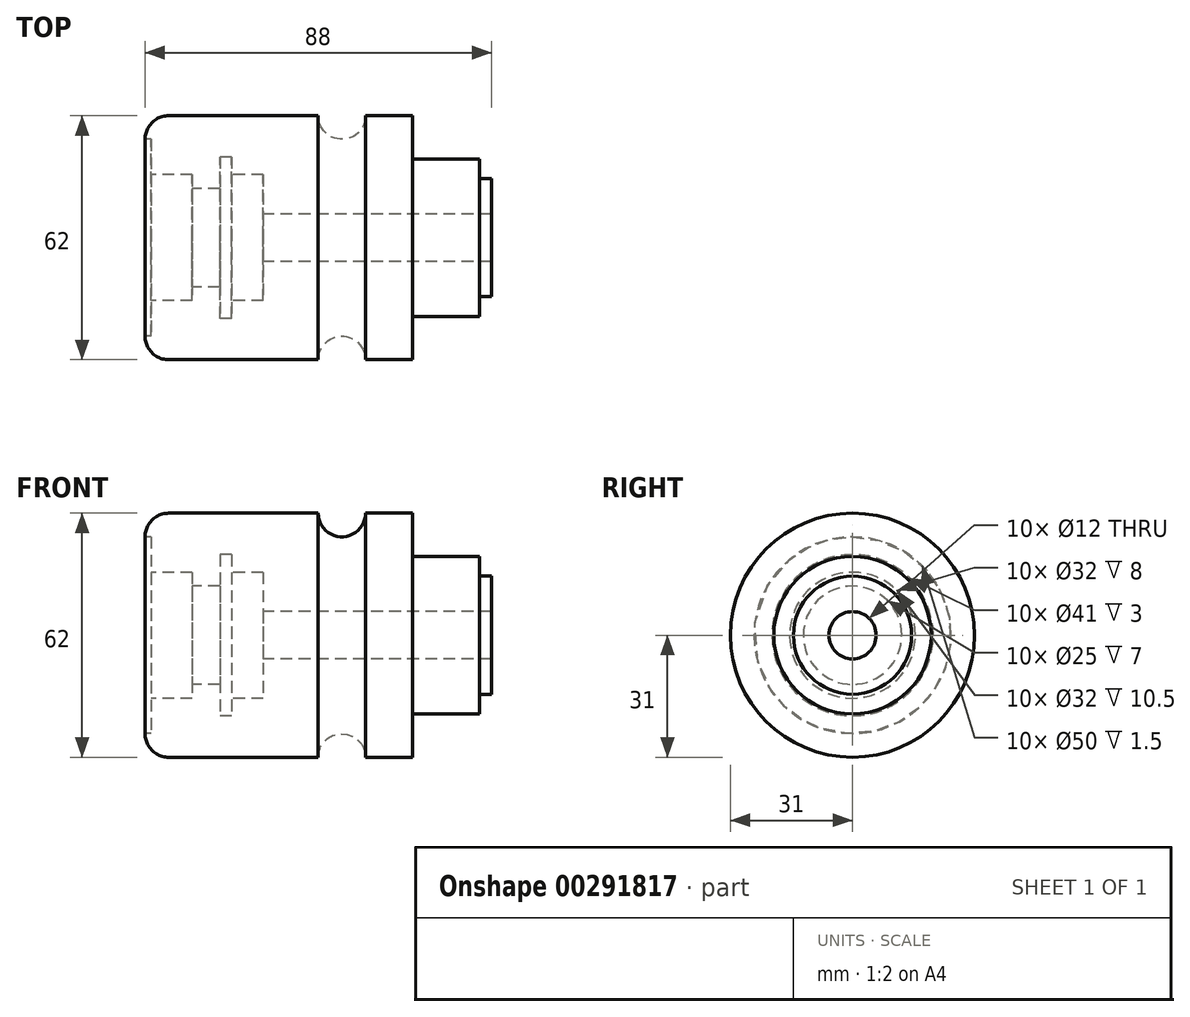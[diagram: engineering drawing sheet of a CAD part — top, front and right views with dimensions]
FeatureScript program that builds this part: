
annotation { "Feature Type Name" : "Feature", "Feature Type Description" : "" }
export const myFeature = defineFeature(function(context is Context, id is Id, definition is map)
    precondition{}
    {
        {
            var Q0;
            Q0=qCreatedBy(makeId("Front.planeOp"),FACE);
            var sketch = newSketch(context, id + "F0", { "sketchPlane" : qUnion([Q0])});
            skLineSegment(sketch, "E0", {"start": v(0, 0) * mm, "end": v(90.92, 0) * mm, "construction": true});
            skLineSegment(sketch, "E1", {"start": v(0, 0) * mm, "end": v(0, 31) * mm});
            skLineSegment(sketch, "E2", {"start": v(0, 31) * mm, "end": v(44, 31) * mm});
            skLineSegment(sketch, "E3", {"start": v(68, 31) * mm, "end": v(68, 20) * mm});
            skLineSegment(sketch, "E4", {"start": v(68, 20) * mm, "end": v(85, 20) * mm});
            skLineSegment(sketch, "E5", {"start": v(85, 20) * mm, "end": v(85, 15) * mm});
            skLineSegment(sketch, "E6", {"start": v(85, 15) * mm, "end": v(88, 15) * mm});
            skLineSegment(sketch, "E7", {"start": v(88, 15) * mm, "end": v(88, 0) * mm});
            skArc(sketch, "E8", {"start": v(44, 31) * mm, "mid": v(50, 25) * mm, "end": v(56, 31) * mm});
            skLineSegment(sketch, "E9.trimOffspring", {"start": v(56, 31) * mm, "end": v(68, 31) * mm});
            skLineSegment(sketch, "E10", {"start": v(88, 0) * mm, "end": v(0, 0) * mm});
            skSolve(sketch);
        }
        {
            var Q0;
            Q0 = qSketchRegion(id + "F0", true);
            var Q1;
            Q1=sQuery(id+"F0.wireOp",EDGE,"E0");
            revolve(context, id + "F1", {"entities" : qUnion([Q0]), "axis" : qUnion([Q1]), "revolveType" : RevolveType.FULL});
        }
        {
            var Q0;
            Q0=qCreatedBy(makeId("Front.planeOp"),FACE);
            var sketch = newSketch(context, id + "F2", { "sketchPlane" : qUnion([Q0])});
            skLineSegment(sketch, "E11", {"start": v(0, 0) * mm, "end": v(0, 25) * mm});
            skLineSegment(sketch, "E12", {"start": v(0, 25) * mm, "end": v(1.5, 25) * mm});
            skLineSegment(sketch, "E13", {"start": v(1.5, 25) * mm, "end": v(1.5, 16) * mm});
            skLineSegment(sketch, "E14", {"start": v(1.5, 16) * mm, "end": v(12, 16) * mm});
            skLineSegment(sketch, "E15", {"start": v(12, 16) * mm, "end": v(12, 12.5) * mm});
            skLineSegment(sketch, "E16", {"start": v(12, 12.5) * mm, "end": v(19, 12.5) * mm});
            skLineSegment(sketch, "E17", {"start": v(19, 12.5) * mm, "end": v(19, 20.5) * mm});
            skLineSegment(sketch, "E18", {"start": v(19, 20.5) * mm, "end": v(22, 20.5) * mm});
            skLineSegment(sketch, "E19", {"start": v(22, 20.5) * mm, "end": v(22, 16) * mm});
            skLineSegment(sketch, "E20", {"start": v(22, 16) * mm, "end": v(30, 16) * mm});
            skLineSegment(sketch, "E21", {"start": v(30, 16) * mm, "end": v(30, 6) * mm});
            skLineSegment(sketch, "E22", {"start": v(30, 6) * mm, "end": v(88, 6) * mm});
            skLineSegment(sketch, "E23", {"start": v(88, 6) * mm, "end": v(88, 0) * mm});
            skLineSegment(sketch, "E24", {"start": v(88, 0) * mm, "end": v(0, 0) * mm});
            skLineSegment(sketch, "E25", {"start": v(0, 0) * mm, "end": v(-15.84, 0) * mm, "construction": true});
            skSolve(sketch);
        }
        {
            var Q0;
            Q0 = qSketchRegion(id + "F2", true);
            var Q1;
            Q1=sQuery(id+"F2.wireOp",EDGE,"E25");
            revolve(context, id + "F3", {"operationType" : NewBodyOperationType.REMOVE, "entities" : qUnion([Q0]), "axis" : qUnion([Q1]), "revolveType" : RevolveType.FULL, "oppositeDirection" : true});
        }
        {
            var Q0;
            Q0=makeQuery(id+"F1.opRevolve","SWEPT_EDGE",EDGE,{"disambiguationData":[OSD([sQuery(id+"F0.wireOp",EDGE,"E1"),sQuery(id+"F0.wireOp",EDGE,"E2")])]});
            fillet(context, id + "F4", {"entities" : qUnion([Q0]), "radius" : 6 * mm, "tangentPropagation" : true, "allowEdgeOverflow" : false});
        }
    });
